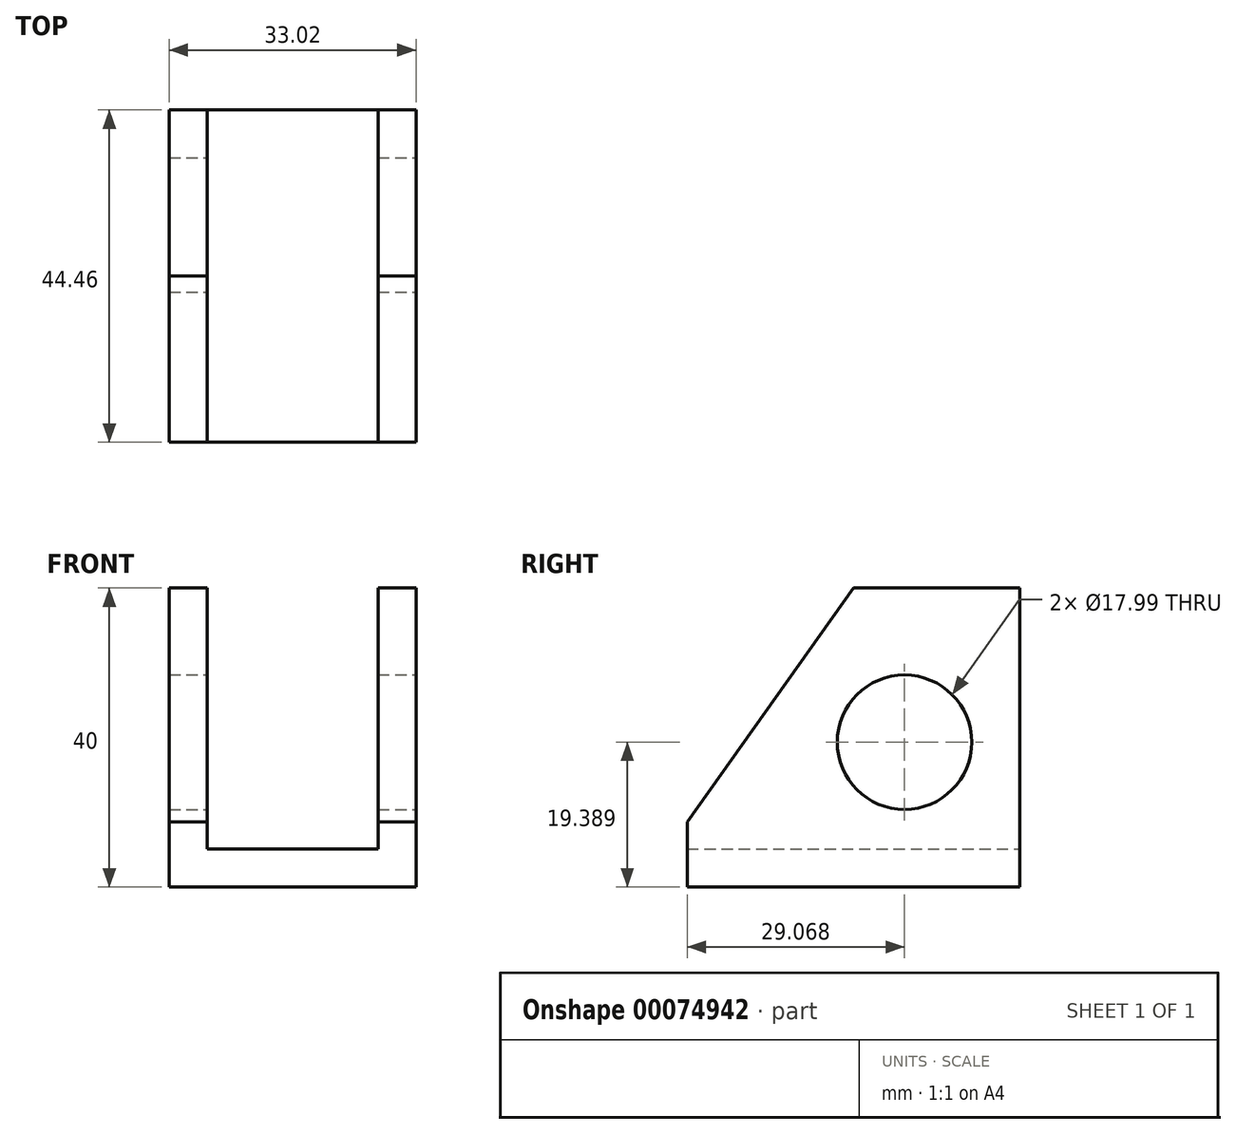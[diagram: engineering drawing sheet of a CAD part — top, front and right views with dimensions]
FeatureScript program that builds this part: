
annotation { "Feature Type Name" : "Feature", "Feature Type Description" : "" }
export const myFeature = defineFeature(function(context is Context, id is Id, definition is map)
    precondition{}
    {
        {
            var Q0;
            Q0=qCreatedBy(makeId("Front.planeOp"),FACE);
            var sketch = newSketch(context, id + "F0", { "sketchPlane" : qUnion([Q0])});
            skLineSegment(sketch, "E0", {"start": v(-16.51, 0) * mm, "end": v(-16.51, 40) * mm});
            skLineSegment(sketch, "E1", {"start": v(-16.51, 40) * mm, "end": v(-11.43, 40) * mm});
            skLineSegment(sketch, "E2", {"start": v(-11.43, 40) * mm, "end": v(-11.43, 5.08) * mm});
            skLineSegment(sketch, "E3", {"start": v(-11.43, 5.08) * mm, "end": v(0, 5.08) * mm});
            skLineSegment(sketch, "E4", {"start": v(-16.51, 0) * mm, "end": v(0, 0) * mm});
            skLineSegment(sketch, "E5.MirrorCS", {"start": v(11.43, 40) * mm, "end": v(11.43, 5.08) * mm});
            skLineSegment(sketch, "E6.MirrorCS", {"start": v(16.51, 0) * mm, "end": v(16.51, 40) * mm});
            skLineSegment(sketch, "E7.MirrorCS", {"start": v(16.51, 0) * mm, "end": v(0, 0) * mm});
            skLineSegment(sketch, "E8.MirrorCS", {"start": v(11.43, 5.08) * mm, "end": v(0, 5.08) * mm});
            skLineSegment(sketch, "E9.MirrorCS", {"start": v(16.51, 40) * mm, "end": v(11.43, 40) * mm});
            skSolve(sketch);
        }
        {
            var Q0;
            Q0=makeQuery(id+"F0.imprint","IMPRINT",FACE,{"disambiguationData":[TD([[makeQuery(id+"F0.imprint","IMPRINT",EDGE,{"derivedFrom":sQuery(id+"F0.wireOp",EDGE,"E0")}),-1.0]])]});
            extrude(context, id + "F1", {"entities" : qUnion([Q0]), "endBound" : BoundingType.SYMMETRIC, "depth" : 44.45 * mm});
        }
        {
            var Q0;
            Q0=makeQuery(id+"F1.opExtrude","SWEPT_FACE",FACE,{"disambiguationData":[OSD([sQuery(id+"F0.wireOp",EDGE,"E6.MirrorCS")])]});
            var sketch = newSketch(context, id + "F2", { "sketchPlane" : qUnion([Q0])});
            skLineSegment(sketch, "E10", {"start": v(-22.23, 8.71) * mm, "end": v(0, 40) * mm});
            skLineSegment(sketch, "E11", {"start": v(0, 40) * mm, "end": v(-22.23, 40) * mm});
            skLineSegment(sketch, "E12", {"start": v(-22.23, 40) * mm, "end": v(-22.23, 8.71) * mm});
            skSolve(sketch);
        }
        {
            var Q0;
            Q0=makeQuery(id+"F2.imprint","IMPRINT",FACE,{"disambiguationData":[TD([[makeQuery(id+"F2.imprint","IMPRINT",EDGE,{"derivedFrom":sQuery(id+"F2.wireOp",EDGE,"E10")}),1.0]])]});
            extrude(context, id + "F3", {"entities" : qUnion([Q0]), "operationType" : NewBodyOperationType.REMOVE, "oppositeDirection" : true, "depth" : 33.02 * mm});
        }
        {
            var Q0;
            Q0=makeQuery(id+"F1.opExtrude","SWEPT_FACE",FACE,{"disambiguationData":[OSD([sQuery(id+"F0.wireOp",EDGE,"E6.MirrorCS")])]});
            var sketch = newSketch(context, id + "F4", { "sketchPlane" : qUnion([Q0])});
            skCircle(sketch, "E13", {"center": v(6.84, 19.39) * mm, "radius": 9 * mm});
            skSolve(sketch);
        }
        {
            var Q0;
            Q0 = qSketchRegion(id + "F4", true);
            extrude(context, id + "F5", {"entities" : qUnion([Q0]), "operationType" : NewBodyOperationType.REMOVE, "endBound" : BoundingType.THROUGH_ALL, "oppositeDirection" : true, "depth" : 33.02 * mm});
        }
    });
